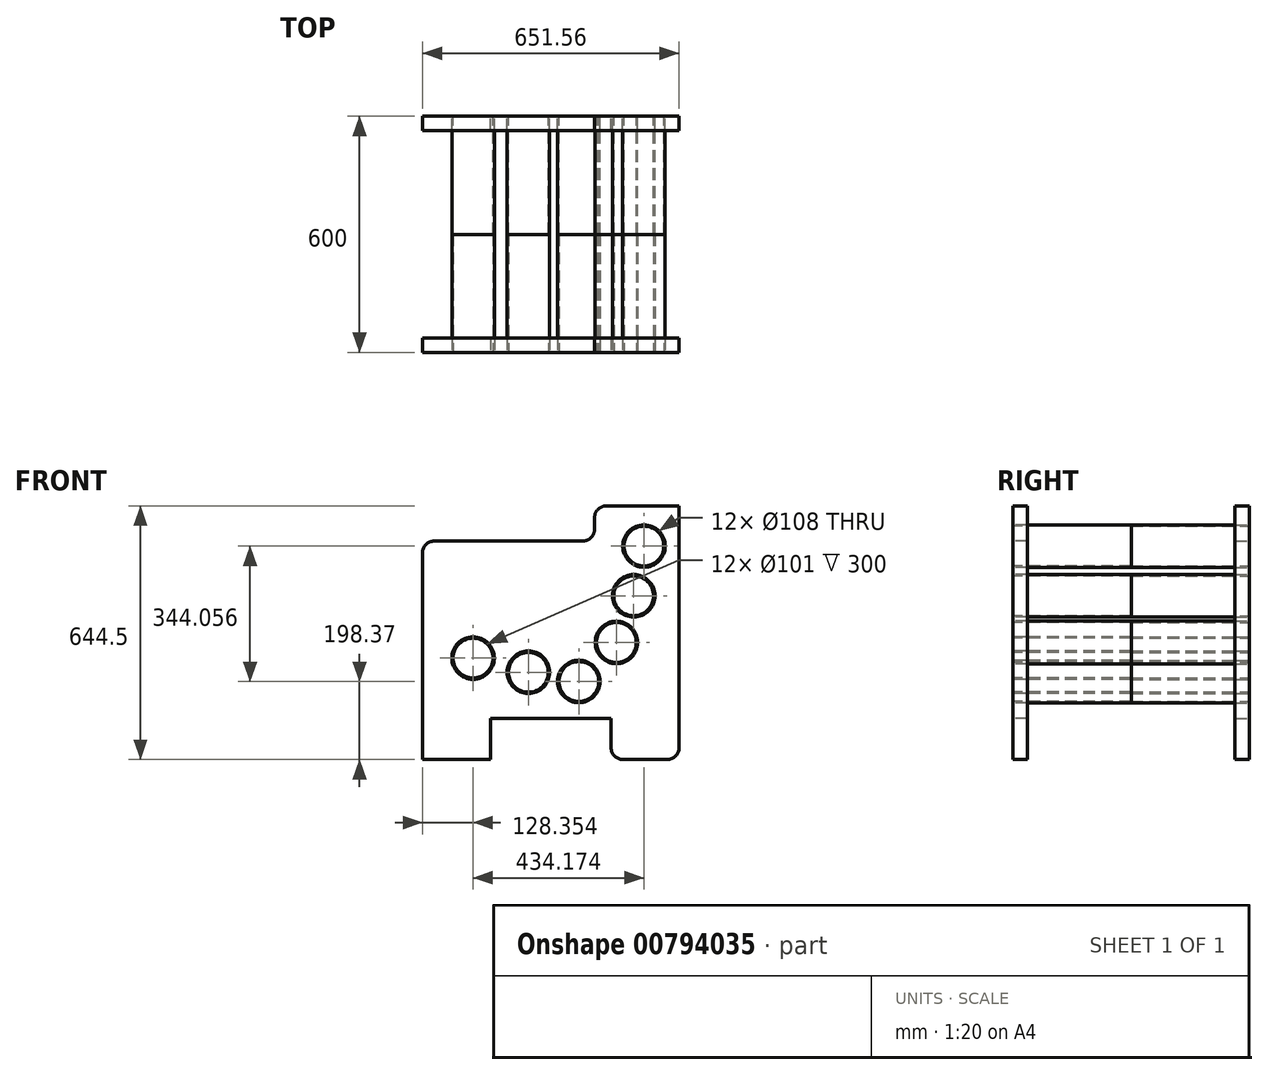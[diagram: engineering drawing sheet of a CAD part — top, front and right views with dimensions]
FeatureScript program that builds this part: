
annotation { "Feature Type Name" : "Feature", "Feature Type Description" : "" }
export const myFeature = defineFeature(function(context is Context, id is Id, definition is map)
    precondition{}
    {
        {
            var Q0;
            Q0=qCreatedBy(makeId("Front.planeOp"),FACE);
            var sketch = newSketch(context, id + "F0", { "sketchPlane" : qUnion([Q0])});
            skCircle(sketch, "E0", {"center": v(2.84, 31.92) * mm, "radius": 54 * mm});
            skCircle(sketch, "E1", {"center": v(-23.27, -94.51) * mm, "radius": 54 * mm});
            skCircle(sketch, "E2", {"center": v(-67.13, -212.92) * mm, "radius": 54 * mm});
            skCircle(sketch, "E3", {"center": v(-162.71, -312.14) * mm, "radius": 54 * mm});
            skCircle(sketch, "E4", {"center": v(-290.7, -288.66) * mm, "radius": 54 * mm});
            skCircle(sketch, "E5.0", {"center": v(2.84, 31.92) * mm, "radius": 50.5 * mm});
            skCircle(sketch, "E6.0", {"center": v(-23.27, -94.51) * mm, "radius": 50.5 * mm});
            skCircle(sketch, "E7.0", {"center": v(-67.13, -212.92) * mm, "radius": 50.5 * mm});
            skCircle(sketch, "E8.0", {"center": v(-162.71, -312.14) * mm, "radius": 50.5 * mm});
            skCircle(sketch, "E9.0", {"center": v(-290.7, -288.66) * mm, "radius": 50.5 * mm});
            skCircle(sketch, "E10", {"center": v(-431.34, -252.6) * mm, "radius": 54 * mm});
            skCircle(sketch, "E11.0", {"center": v(-431.34, -252.6) * mm, "radius": 50.5 * mm});
            skLineSegment(sketch, "E12", {"start": v(91.87, 134) * mm, "end": v(91.87, -405.51) * mm});
            skLineSegment(sketch, "E13", {"start": v(-80.55, -405.51) * mm, "end": v(-386.82, -405.51) * mm});
            skLineSegment(sketch, "E14", {"start": v(-559.69, -405.51) * mm, "end": v(-559.69, 44.8) * mm});
            skLineSegment(sketch, "E15", {"start": v(-559.69, 44.8) * mm, "end": v(-122.62, 44.8) * mm});
            skLineSegment(sketch, "E16", {"start": v(-122.67, 45.56) * mm, "end": v(-122.67, 129) * mm});
            skLineSegment(sketch, "E17", {"start": v(-117.67, 134) * mm, "end": v(91.87, 134) * mm});
            skPoint(sketch, "E18.orphan", {"position": v(91.87, 144.36) * mm});
            skPoint(sketch, "E19.visualSharp", {"position": v(-122.67, 134) * mm});
            skLineSegment(sketch, "E20", {"start": v(91.87, -405.51) * mm, "end": v(91.87, -510.51) * mm});
            skLineSegment(sketch, "E21", {"start": v(91.87, -510.51) * mm, "end": v(-80.55, -510.51) * mm});
            skLineSegment(sketch, "E22", {"start": v(-80.55, -510.51) * mm, "end": v(-80.55, -405.51) * mm});
            skLineSegment(sketch, "E23", {"start": v(-559.69, -405.51) * mm, "end": v(-559.69, -510.51) * mm});
            skLineSegment(sketch, "E24", {"start": v(-559.69, -510.51) * mm, "end": v(-386.82, -510.51) * mm});
            skLineSegment(sketch, "E25", {"start": v(-386.82, -510.51) * mm, "end": v(-386.82, -405.51) * mm});
            skLineSegment(sketch, "E26", {"start": v(-122.67, 129) * mm, "end": v(-122.67, 134) * mm});
            skLineSegment(sketch, "E27", {"start": v(-117.67, 134) * mm, "end": v(-122.67, 134) * mm});
            skLineSegment(sketch, "E28", {"start": v(-122.67, 134) * mm, "end": v(91.87, 134) * mm});
            skLineSegment(sketch, "E29", {"start": v(91.87, 134) * mm, "end": v(91.87, -510.51) * mm});
            skLineSegment(sketch, "E30", {"start": v(-386.82, -405.51) * mm, "end": v(-386.82, -510.51) * mm});
            skLineSegment(sketch, "E31", {"start": v(-386.82, -510.51) * mm, "end": v(-559.69, -510.51) * mm});
            skLineSegment(sketch, "E32", {"start": v(-559.69, -510.51) * mm, "end": v(-559.69, 44.8) * mm});
            skLineSegment(sketch, "E33", {"start": v(-122.62, 44.8) * mm, "end": v(-122.67, 134) * mm});
            skSolve(sketch);
        }
        {
            var Q0;
            Q0=makeQuery(id+"F0.imprint","IMPRINT",FACE,{"disambiguationData":[TD([[makeQuery(id+"F0.imprint","IMPRINT",EDGE,{"derivedFrom":sQuery(id+"F0.wireOp",EDGE,"E0")}),1.0]])]});
            var Q1;
            Q1=makeQuery(id+"F0.imprint","IMPRINT",FACE,{"disambiguationData":[TD([[makeQuery(id+"F0.imprint","IMPRINT",EDGE,{"derivedFrom":sQuery(id+"F0.wireOp",EDGE,"E1")}),1.0]])]});
            var Q2;
            Q2=makeQuery(id+"F0.imprint","IMPRINT",FACE,{"disambiguationData":[TD([[makeQuery(id+"F0.imprint","IMPRINT",EDGE,{"derivedFrom":sQuery(id+"F0.wireOp",EDGE,"E2")}),1.0]])]});
            var Q3;
            Q3=makeQuery(id+"F0.imprint","IMPRINT",FACE,{"disambiguationData":[TD([[makeQuery(id+"F0.imprint","IMPRINT",EDGE,{"derivedFrom":sQuery(id+"F0.wireOp",EDGE,"E3")}),1.0]])]});
            var Q4;
            Q4=makeQuery(id+"F0.imprint","IMPRINT",FACE,{"disambiguationData":[TD([[makeQuery(id+"F0.imprint","IMPRINT",EDGE,{"derivedFrom":sQuery(id+"F0.wireOp",EDGE,"E4")}),1.0]])]});
            var Q5;
            Q5=makeQuery(id+"F0.imprint","IMPRINT",FACE,{"disambiguationData":[TD([[makeQuery(id+"F0.imprint","IMPRINT",EDGE,{"derivedFrom":sQuery(id+"F0.wireOp",EDGE,"E10")}),1.0]])]});
            extrude(context, id + "F1", {"entities" : qUnion([Q0, Q1, Q2, Q3, Q4, Q5]), "depth" : 300 * mm, "offsetDistance" : 25 * mm});
        }
        {
            var Q0;
            Q0=makeQuery(id+"F0.imprint","IMPRINT",FACE,{"disambiguationData":[TD([[makeQuery(id+"F0.imprint","IMPRINT",EDGE,{"derivedFrom":sQuery(id+"F0.wireOp",EDGE,"E0")}),-1.0]])]});
            extrude(context, id + "F2", {"entities" : qUnion([Q0]), "depth" : 36 * mm, "offsetDistance" : 25 * mm});
        }
        {
            var Q0;
            Q0=makeQuery(id+"F2.opExtrude","SWEPT_EDGE",EDGE,{"disambiguationData":[OSD([sQuery(id+"F0.wireOp",EDGE,"E28"),sQuery(id+"F0.wireOp",EDGE,"E33")])]});
            var Q1;
            Q1=makeQuery(id+"F2.opExtrude","SWEPT_EDGE",EDGE,{"disambiguationData":[OSD([sQuery(id+"F0.wireOp",EDGE,"E32"),sQuery(id+"F0.wireOp",EDGE,"E15")])]});
            var Q2;
            Q2=makeQuery(id+"F2.opExtrude","SWEPT_EDGE",EDGE,{"disambiguationData":[OSD([sQuery(id+"F0.wireOp",EDGE,"E31"),sQuery(id+"F0.wireOp",EDGE,"E32")])]});
            var Q3;
            Q3=makeQuery(id+"F2.opExtrude","SWEPT_EDGE",EDGE,{"disambiguationData":[OSD([sQuery(id+"F0.wireOp",EDGE,"E30"),sQuery(id+"F0.wireOp",EDGE,"E31")])]});
            var Q4;
            Q4=makeQuery(id+"F2.opExtrude","SWEPT_EDGE",EDGE,{"disambiguationData":[OSD([sQuery(id+"F0.wireOp",EDGE,"E21"),sQuery(id+"F0.wireOp",EDGE,"E22")])]});
            var Q5;
            Q5=makeQuery(id+"F2.opExtrude","SWEPT_EDGE",EDGE,{"disambiguationData":[OSD([sQuery(id+"F0.wireOp",EDGE,"E22"),sQuery(id+"F0.wireOp",EDGE,"E13")])]});
            var Q6;
            Q6=makeQuery(id+"F2.opExtrude","SWEPT_EDGE",EDGE,{"disambiguationData":[OSD([sQuery(id+"F0.wireOp",EDGE,"E13"),sQuery(id+"F0.wireOp",EDGE,"E30")])]});
            var Q7;
            Q7=makeQuery(id+"F2.opExtrude","SWEPT_EDGE",EDGE,{"disambiguationData":[OSD([sQuery(id+"F0.wireOp",EDGE,"E29"),sQuery(id+"F0.wireOp",EDGE,"E21")])]});
            var Q8;
            Q8=makeQuery(id+"F2.opExtrude","SWEPT_EDGE",EDGE,{"disambiguationData":[OSD([sQuery(id+"F0.wireOp",EDGE,"E28"),sQuery(id+"F0.wireOp",EDGE,"E29")])]});
            fillet(context, id + "F3", {"entities" : qUnion([Q0, Q1, Q2, Q3, Q4, Q5, Q6, Q7, Q8]), "radius" : 30 * mm, "tangentPropagation" : true, "allowEdgeOverflow" : false});
        }
        {
            var Q0;
            Q0=makeQuery(id+"F1.opExtrude","SWEPT_BODY",BODY,{"disambiguationData":[OSD([sQuery(id+"F0.wireOp",EDGE,"E3"),sQuery(id+"F0.wireOp",EDGE,"E8.0")])]});
            var Q1;
            Q1=makeQuery(id+"F1.opExtrude","SWEPT_BODY",BODY,{"disambiguationData":[OSD([sQuery(id+"F0.wireOp",EDGE,"E1"),sQuery(id+"F0.wireOp",EDGE,"E6.0")])]});
            var Q2;
            Q2=makeQuery(id+"F2.opExtrude","SWEPT_BODY",BODY,{"disambiguationData":[OSD([sQuery(id+"F0.wireOp",EDGE,"E0"),sQuery(id+"F0.wireOp",EDGE,"E1"),sQuery(id+"F0.wireOp",EDGE,"E2"),sQuery(id+"F0.wireOp",EDGE,"E3"),sQuery(id+"F0.wireOp",EDGE,"E4"),sQuery(id+"F0.wireOp",EDGE,"E10"),sQuery(id+"F0.wireOp",EDGE,"E28"),sQuery(id+"F0.wireOp",EDGE,"E29"),sQuery(id+"F0.wireOp",EDGE,"E21"),sQuery(id+"F0.wireOp",EDGE,"E22"),sQuery(id+"F0.wireOp",EDGE,"E13"),sQuery(id+"F0.wireOp",EDGE,"E30"),sQuery(id+"F0.wireOp",EDGE,"E31"),sQuery(id+"F0.wireOp",EDGE,"E32"),sQuery(id+"F0.wireOp",EDGE,"E15"),sQuery(id+"F0.wireOp",EDGE,"E33")])]});
            var Q3;
            Q3=makeQuery(id+"F1.opExtrude","SWEPT_BODY",BODY,{"disambiguationData":[OSD([sQuery(id+"F0.wireOp",EDGE,"E10"),sQuery(id+"F0.wireOp",EDGE,"E11.0")])]});
            var Q4;
            Q4=makeQuery(id+"F1.opExtrude","SWEPT_BODY",BODY,{"disambiguationData":[OSD([sQuery(id+"F0.wireOp",EDGE,"E4"),sQuery(id+"F0.wireOp",EDGE,"E9.0")])]});
            var Q5;
            Q5=makeQuery(id+"F1.opExtrude","SWEPT_BODY",BODY,{"disambiguationData":[OSD([sQuery(id+"F0.wireOp",EDGE,"E0"),sQuery(id+"F0.wireOp",EDGE,"E5.0")])]});
            var Q6;
            Q6=makeQuery(id+"F1.opExtrude","SWEPT_BODY",BODY,{"disambiguationData":[OSD([sQuery(id+"F0.wireOp",EDGE,"E2"),sQuery(id+"F0.wireOp",EDGE,"E7.0")])]});
            var Q7;
            Q7=makeQuery(id+"F1.opExtrude","CAP_FACE",FACE,{"disambiguationData":[OSD([sQuery(id+"F0.wireOp",EDGE,"E1"),sQuery(id+"F0.wireOp",EDGE,"E6.0")])],"isStart":false});
            mirror(context, id + "F4", {"entities" : qUnion([Q0, Q1, Q2, Q3, Q4, Q5, Q6]), "mirrorPlane" : qUnion([Q7])});
        }
    });
